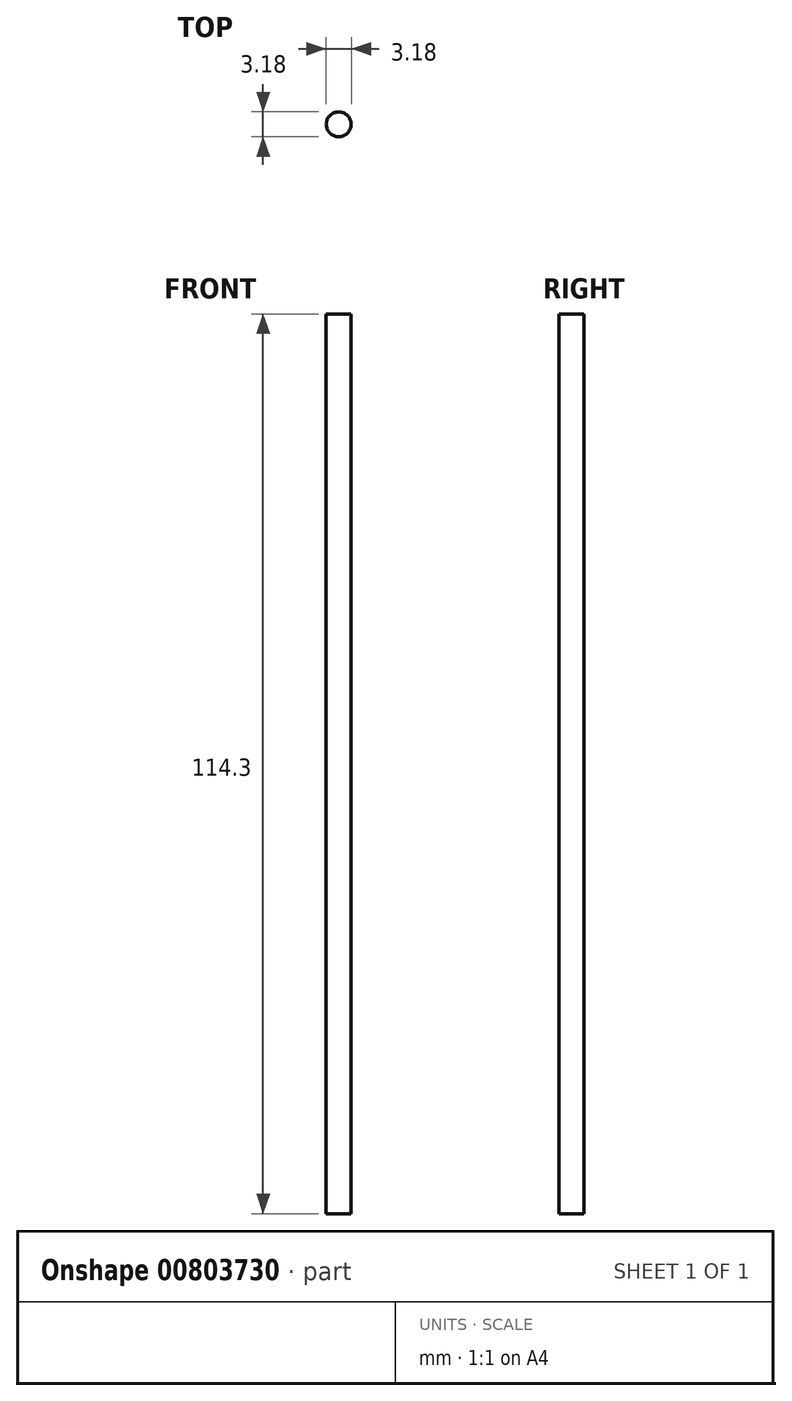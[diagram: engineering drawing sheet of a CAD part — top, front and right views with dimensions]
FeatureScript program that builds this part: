
annotation { "Feature Type Name" : "Feature", "Feature Type Description" : "" }
export const myFeature = defineFeature(function(context is Context, id is Id, definition is map)
    precondition{}
    {
        {
            var Q0;
            Q0=qCreatedBy(makeId("Top.planeOp"),FACE);
            var sketch = newSketch(context, id + "F0", { "sketchPlane" : qUnion([Q0])});
            skCircle(sketch, "E0", {"center": v(0, 0) * mm, "radius": 1.59 * mm});
            skSolve(sketch);
        }
        {
            var Q0;
            Q0=makeQuery(id+"F0.imprint","IMPRINT",FACE,{"disambiguationData":[TD([[makeQuery(id+"F0.imprint","IMPRINT",EDGE,{"derivedFrom":sQuery(id+"F0.wireOp",EDGE,"E0")}),1.0]])]});
            extrude(context, id + "F1", {"entities" : qUnion([Q0]), "depth" : 114.3 * mm, "offsetDistance" : 25.4 * mm});
        }
    });
